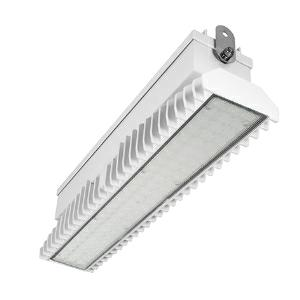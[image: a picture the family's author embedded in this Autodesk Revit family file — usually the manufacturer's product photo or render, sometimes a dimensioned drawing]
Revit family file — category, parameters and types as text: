
# Revit family: 3f_filippi_-_3f_lem_ampio_3f_filippi_-_58881_a0812_-_3f_lem_1_led_50_cr_ampio___vs_e376
name_source: partatom
category: Lighting Fixtures
units: mm (PartAtom-declared; Revit-internal decimal feet)

## family parameters
Cut with Voids When Loaded = No
Host = Face
Light Source = No
Part Type = Normal
Room Calculation Point = No
Round Connector Dimension = Use Diameter
Shared = No

## types (1)
- 3F Filippi - 3F LEM Ampio (1 x LED, 6652 lm, 56 W, 4000 K)
    Apparent Load = 56 VA
    Approval mark = CE
    CIE Flux Codes = 67 90 97 100 100
    Color Rendering = 80
    Color Temperature = 4000 K
    Control Gear = Electronic ballast
    Default Elevation = 1800 mm
    Description = Industrial luminaire with high light output and high luminous efficiency designed with the most innovative technologies for environments with temperature up to 55°C.

ILLUMINOTECHNICAL
Luminous efficiency 100% (DLOR 98%, ULOR 2%).
Initial luminous flux of the luminaire 6652 lm.
Direct symmetric wide distribution: the illuminated area has a rectangular shape.
Installation Interdistance Transv.D = 1.24 x hu - Long.D = 1.20 x hu.
Tabular UGR (CIE 117 - 4H-8H; S=0.25H; 70/50/20): RUG 25.9 - 25.7.
Beam angle: 82° - 83°.
Luminous efficacy 119 lm/W.
Lifetime (L93/B10): 30000 h. (tq+25°C)
Lifetime (L90/B10): 50000 h. (tq+25°C)
Lifetime (L85/B10): 80000 h. (tq+25°C)
Lifetime (L80/B10): 100000 h. (tq+25°C)
Lifetime (L85/B10): 50000 h. (tq+55°C)
Sudden decreased luminous flux after 50000 hours: 0% (C0).
Photobiological safety in compliance with IEC/TR 62778: RG0 risk exempt, (IEC 62471).
In compliance with IEC/EN 62722-2-1 - IEC/EN 62717 standards.

SOURCE
Mid-Power linear LED module 50W/840.
Energy efficiency class (UE 2019/2020 - UE 2019/2015): C.
CIE 13.3 Colour rendering index: CRI >80 (R9 <50%).
IES TM-30 Fidelity Index: Rf = 84 Rg = 95.
CCT nominal colour temperature 4000 K.
Colour initial tolerance (MacAdam): SDCM 3.

MECHANICAL
Passive modular heatsinks in die-casted aluminium, painted in white colour.
To optimize the thermal management of the LED module, the heatsinks are oversized and provided with self-cleaning of cooling fins.
Wiring body in aluminium and galvanised steel anchored solidly to the sinks and thermally separated.
3F Lens lenses with high luminous efficiency, transparent methacrylate (PMMA), fixed to the LED modules.
Fixing brackets in stainless steel.
Luminaire with limited surface temperature. - D - (EN 60598-2-24)
Dimensions: 542x115 mm, height 154 mm. Weight 6.375 kg.
IP65 protection degree.
Mechanical strength to impacts IK06 (1 joule).
Glow-wire test resistance 650°C.

ELECTRICAL
Halogen Free electronic wiring 230V-50/60Hz, power factor 0.95, THD <25%, constant output current, class I, 1 driver.
Power of the luminaire 56 W.
ENEC - CE.
SAFE FLICKER: PstLM=<1 and SVM=<0.4 (IEC TR 61547-1 and IEC TR 63158), to ensure a more comfortable and safe light.
Luminaire compliant with EN 60598-2-22 for power supply from a centralised emergency system CPSS (Central Power Supply System), not incorporated in the luminaire - high risk areas excluded. The default power and flux are 100% in AC and 100% in DC.
Ambient temperature from -30°C to +55°C.
Temperature class T6 max 85°C.
Quick connection via M20 3P connector with 9-13 mm tightening range.
Power unit positioned on a separate compartment by the LED module to ensure optimum temperatures of cabling components, to be inspectable and maintainable.
Relative humidity UR: <85%.

INSTALLATION
Ceiling / Suspended / Wall.
All accessories dedicated to this product are available on the Catalog and on our website www.3F-Filippi.com.

ACCESSORIES
A0812 - Anti-glare microprismatic VS moulded glass, tempered, not flammable, with sealing gasket.
One required for each light module. The pack contains 10 pieces.

APPLICATIONS
In commercial environments, exhibition and industrial areas, stores, open areas.
Applications with high ambient temperature up to 55°C.
Environments in which it is necessary a total protection against falling fragments (eg environments with foodstuffs or machines with moving parts or with extreme temperature changes), use luminaires with polycarbonate lenses.

WARNING
Fixture not suitable for cold stores with an ambient temperature <0°C and/or relative humidity >85%.
Luminaire designed for disposal/recycling at end-of-life.
Replaceable (LED only) light source by a professional. Replaceable control gear by a professional.
    Height = 154 mm
    Lamp = 1 x LED
    Lamp Light Flux = 6652 lm
    Lamp Power = 56 W
    Lamp count = 1
    Length = 542 mm
    Lifetime = 50000 h
    Luminous efficacy = 119 lm/W
    Manufacturer = 3F Filippi
    ModVariant = No
    Model = 3F Filippi - 58881+A0812 - 3F LEM 1 LED 50 CR AMPIO + VS
    Mounting Place = Ceiling
    Mounting Type = Pendant
    Number of Poles = 1
    OnlyDefault = Yes
    Power Factor = 1
    Product Name = 3F Filippi - 3F LEM Ampio
    Product group = pendant luminaire
    ProductGroupID = 9
    Protection Class = Protection class I
    Protection Degree = IP 65
    RLX_Detail_Level = 1
    RLX_Emergency_Light_Flux = 0 lm
    RLX_Emergency_Type = 0
    RLX_Emergency_Type_DB = No
    RlxData = <blob elided: 90485 chars, md5=15659828>
    Socket = socket
    Standby Power = 0 W
    System Light Flux = 6652 lm
    System Power = 56 W
    Type Comments = Product without accessories
    Type Image = 3f_filippi_-_lem_1__a0812.jpg
    URL = http://relux.com
    VarID = ---
    Voltage = 0 V
    Weight = 0.00 kg
    Width = 115 mm

## geometry (parser evidence)
native form markers: Blend x4, Sweep x12
no freeform markers — native parametric forms only
